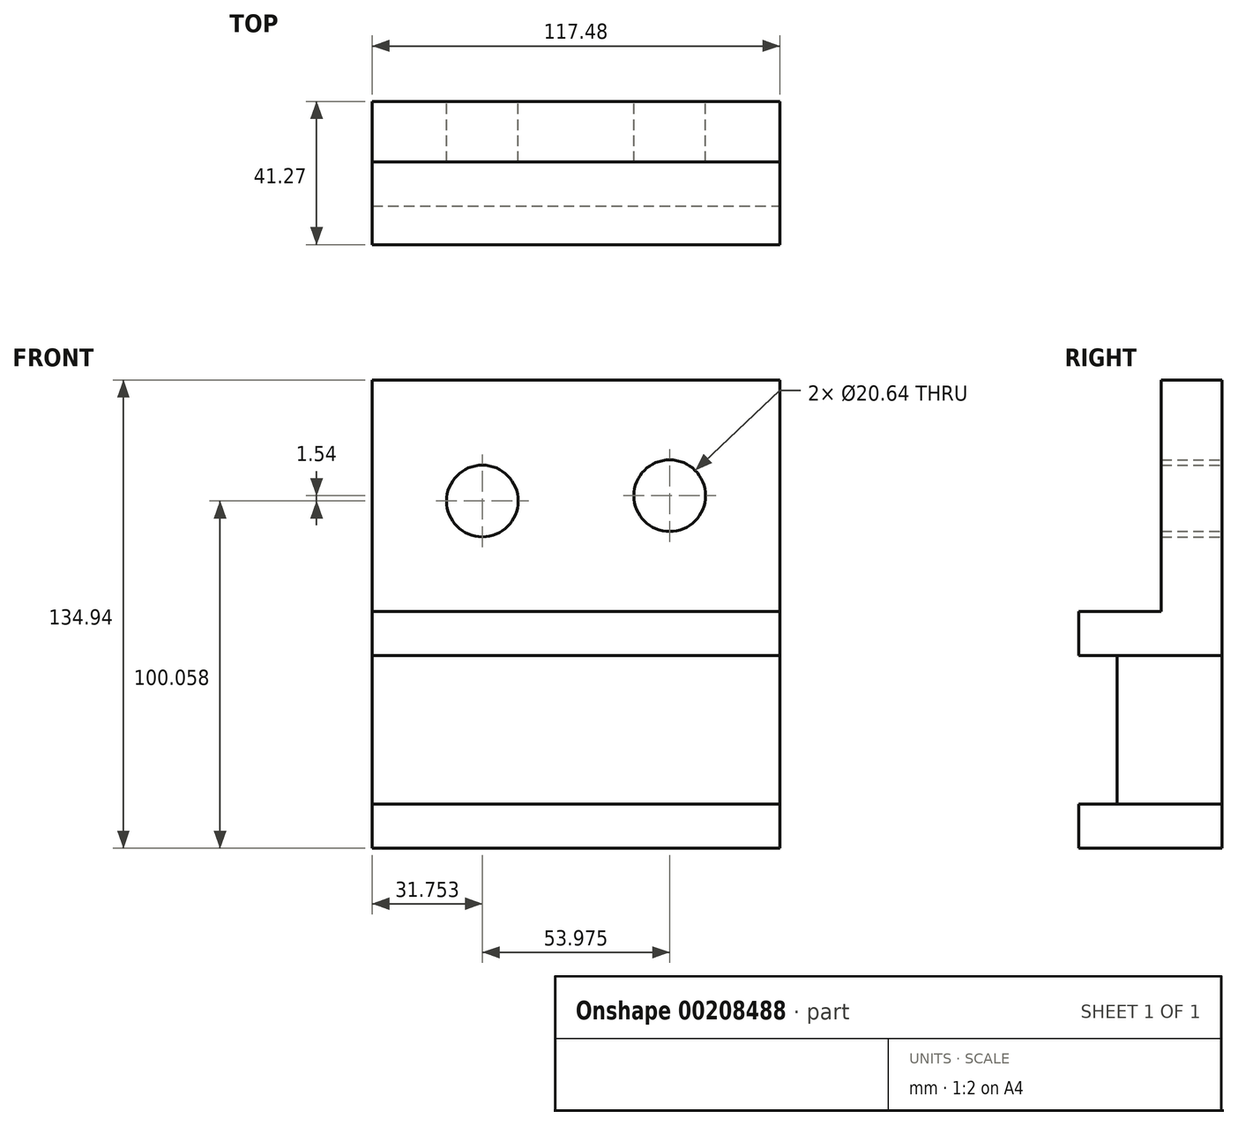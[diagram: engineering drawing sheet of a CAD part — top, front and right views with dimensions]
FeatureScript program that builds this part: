
annotation { "Feature Type Name" : "Feature", "Feature Type Description" : "" }
export const myFeature = defineFeature(function(context is Context, id is Id, definition is map)
    precondition{}
    {
        {
            var Q0;
            Q0=qCreatedBy(makeId("Front.planeOp"),FACE);
            var sketch = newSketch(context, id + "F0", { "sketchPlane" : qUnion([Q0])});
            skLineSegment(sketch, "E0.MirrorCS", {"start": v(58.74, 79.38) * mm, "end": v(-4.76, 79.38) * mm});
            skLineSegment(sketch, "E1", {"start": v(58.74, 79.38) * mm, "end": v(58.74, 12.7) * mm});
            skLineSegment(sketch, "E2.MirrorCS", {"start": v(-58.74, 79.38) * mm, "end": v(-58.74, 12.7) * mm});
            skLineSegment(sketch, "E3", {"start": v(-58.74, 12.7) * mm, "end": v(58.74, 12.7) * mm});
            skLineSegment(sketch, "E4", {"start": v(58.74, 79.38) * mm, "end": v(26.99, 79.38) * mm, "construction": true});
            skCircle(sketch, "E5", {"center": v(26.99, 46.04) * mm, "radius": 10.32 * mm});
            skCircle(sketch, "E6.MirrorC", {"center": v(-26.99, 44.5) * mm, "radius": 10.32 * mm});
            skPoint(sketch, "E7.orphan", {"position": v(-58.74, 46.04) * mm});
            skPoint(sketch, "E8.end.orphan", {"position": v(0, 12.7) * mm});
            skPoint(sketch, "E9.orphan", {"position": v(26.99, 12.7) * mm});
            skPoint(sketch, "E10.trimOffspring.end.orphan", {"position": v(58.74, 46.04) * mm});
            skLineSegment(sketch, "E11", {"start": v(-58.74, 12.7) * mm, "end": v(-58.74, 0) * mm});
            skPoint(sketch, "E12.end.orphan", {"position": v(0, 77.84) * mm});
            skLineSegment(sketch, "E13", {"start": v(-58.74, 79.38) * mm, "end": v(-4.76, 79.38) * mm});
            skLineSegment(sketch, "E14.MirrorCS", {"start": v(58.74, 12.7) * mm, "end": v(58.74, 0) * mm});
            skLineSegment(sketch, "E15", {"start": v(-58.74, 0) * mm, "end": v(58.74, 0) * mm});
            skLineSegment(sketch, "E16", {"start": v(58.74, 0) * mm, "end": v(58.74, -42.86) * mm});
            skLineSegment(sketch, "E17.MirrorCS", {"start": v(-58.74, 0) * mm, "end": v(-58.74, -42.86) * mm});
            skLineSegment(sketch, "E18", {"start": v(-58.74, -42.86) * mm, "end": v(58.74, -42.86) * mm});
            skPoint(sketch, "E19.end.orphan", {"position": v(0, -42.86) * mm});
            skLineSegment(sketch, "E20.MirrorCS", {"start": v(-58.74, -55.56) * mm, "end": v(58.74, -55.56) * mm});
            skLineSegment(sketch, "E21.MirrorCS", {"start": v(-58.74, -55.56) * mm, "end": v(-58.74, -42.86) * mm});
            skLineSegment(sketch, "E22.MirrorCS", {"start": v(58.74, -55.56) * mm, "end": v(58.74, -42.86) * mm});
            skPoint(sketch, "E23.end.orphan", {"position": v(58.74, -21.43) * mm});
            skPoint(sketch, "E23.start.orphan", {"position": v(-58.74, -21.43) * mm});
            skSolve(sketch);
        }
        {
            var Q0;
            Q0=makeQuery(id+"F0.imprint","IMPRINT",FACE,{"disambiguationData":[TD([[makeQuery(id+"F0.imprint","IMPRINT",EDGE,{"derivedFrom":sQuery(id+"F0.wireOp",EDGE,"E0.MirrorCS")}),1.0]])]});
            extrude(context, id + "F1", {"entities" : qUnion([Q0]), "depth" : 17.46 * mm});
        }
        {
            var Q0;
            Q0=makeQuery(id+"F0.imprint","IMPRINT",FACE,{"disambiguationData":[TD([[makeQuery(id+"F0.imprint","IMPRINT",EDGE,{"derivedFrom":sQuery(id+"F0.wireOp",EDGE,"E3")}),-1.0]])]});
            var Q1;
            Q1=makeQuery(id+"F0.imprint","IMPRINT",FACE,{"disambiguationData":[TD([[makeQuery(id+"F0.imprint","IMPRINT",EDGE,{"derivedFrom":sQuery(id+"F0.wireOp",EDGE,"E18")}),-1.0]])]});
            extrude(context, id + "F2", {"entities" : qUnion([Q0, Q1]), "operationType" : NewBodyOperationType.ADD, "depth" : 41.27 * mm});
        }
        {
            var Q0;
            Q0=makeQuery(id+"F0.imprint","IMPRINT",FACE,{"disambiguationData":[TD([[makeQuery(id+"F0.imprint","IMPRINT",EDGE,{"derivedFrom":sQuery(id+"F0.wireOp",EDGE,"E15")}),-1.0]])]});
            extrude(context, id + "F3", {"entities" : qUnion([Q0]), "depth" : 30.16 * mm});
        }
    });
